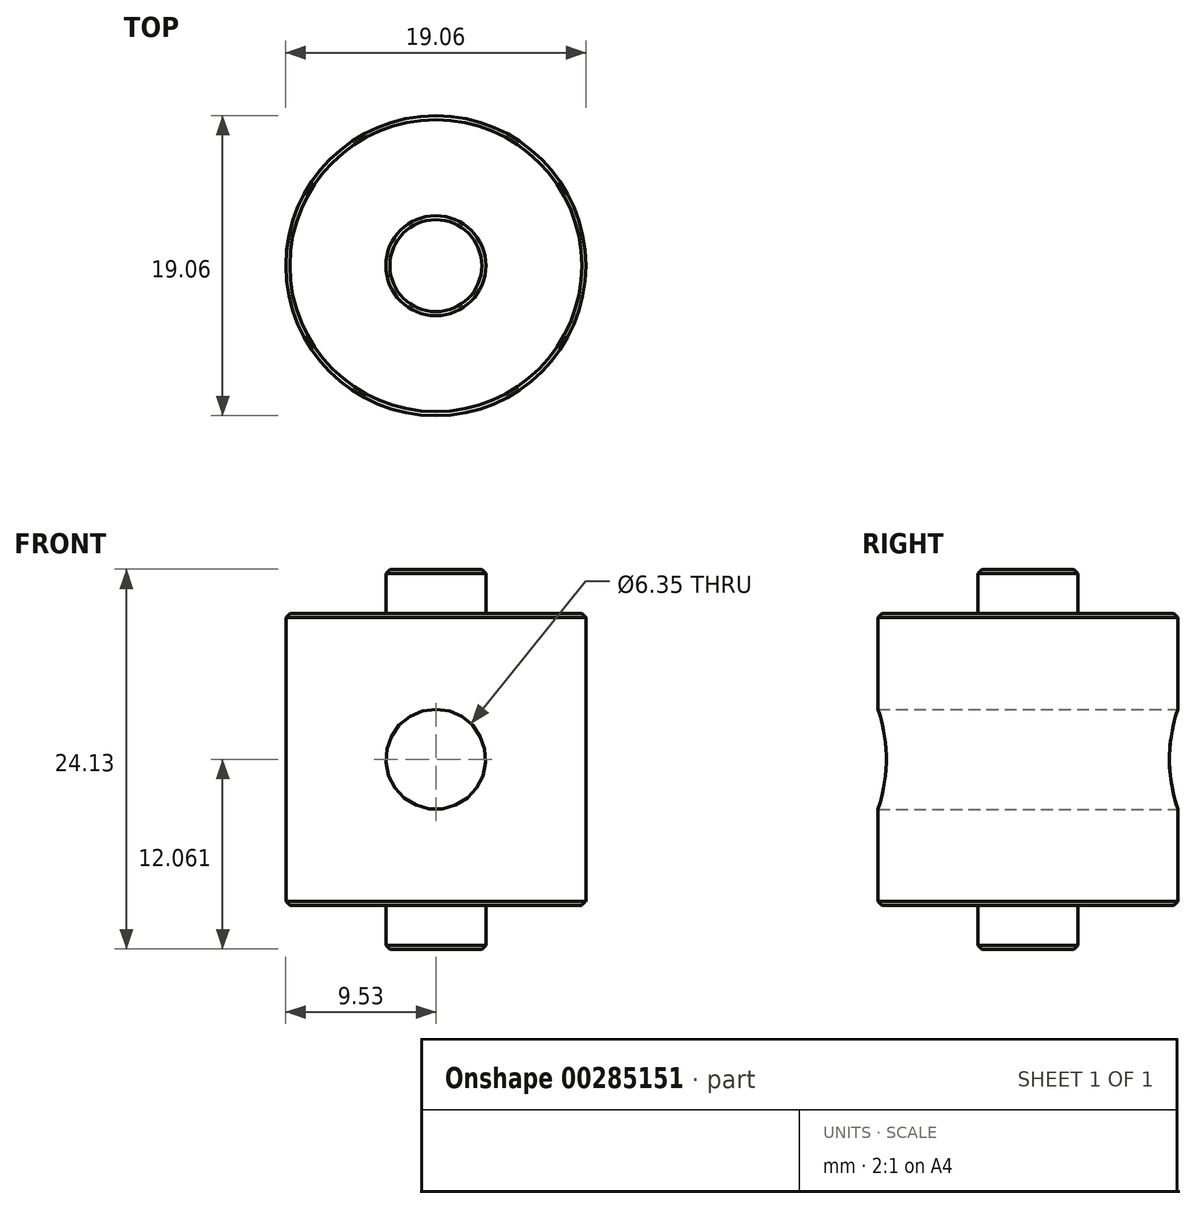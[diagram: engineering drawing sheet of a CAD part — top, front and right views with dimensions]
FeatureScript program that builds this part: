
annotation { "Feature Type Name" : "Feature", "Feature Type Description" : "" }
export const myFeature = defineFeature(function(context is Context, id is Id, definition is map)
    precondition{}
    {
        {
            var Q0;
            Q0=qCreatedBy(makeId("Top.planeOp"),FACE);
            var sketch = newSketch(context, id + "F0", { "sketchPlane" : qUnion([Q0])});
            skCircle(sketch, "E0", {"center": v(0, 0) * mm, "radius": 9.53 * mm});
            skSolve(sketch);
        }
        {
            var Q0;
            Q0=makeQuery(id+"F0.imprint","IMPRINT",FACE,{"disambiguationData":[TD([[makeQuery(id+"F0.imprint","IMPRINT",EDGE,{"derivedFrom":sQuery(id+"F0.wireOp",EDGE,"E0")}),1.0]])]});
            extrude(context, id + "F1", {"entities" : qUnion([Q0]), "depth" : 18.54 * mm});
        }
        {
            var Q0;
            Q0=makeQuery(id+"F1.opExtrude","CAP_FACE",FACE,{"disambiguationData":[OSD([sQuery(id+"F0.wireOp",EDGE,"E0")])],"isStart":false});
            var sketch = newSketch(context, id + "F2", { "sketchPlane" : qUnion([Q0])});
            skCircle(sketch, "E1", {"center": v(0, 0) * mm, "radius": 3.18 * mm});
            skSolve(sketch);
        }
        {
            var Q0;
            Q0=makeQuery(id+"F2.imprint","IMPRINT",FACE,{"disambiguationData":[TD([[makeQuery(id+"F2.imprint","IMPRINT",EDGE,{"derivedFrom":sQuery(id+"F2.wireOp",EDGE,"E1")}),1.0]])]});
            extrude(context, id + "F3", {"entities" : qUnion([Q0]), "operationType" : NewBodyOperationType.ADD, "depth" : 2.8 * mm});
        }
        {
            var Q0;
            Q0=makeQuery(id+"F1.opExtrude","CAP_FACE",FACE,{"disambiguationData":[OSD([sQuery(id+"F0.wireOp",EDGE,"E0")])],"isStart":true});
            var sketch = newSketch(context, id + "F4", { "sketchPlane" : qUnion([Q0])});
            skCircle(sketch, "E2", {"center": v(0, 0) * mm, "radius": 3.18 * mm});
            skSolve(sketch);
        }
        {
            var Q0;
            Q0 = qSketchRegion(id + "F4", true);
            extrude(context, id + "F5", {"entities" : qUnion([Q0]), "operationType" : NewBodyOperationType.ADD, "depth" : 2.8 * mm});
        }
        {
            var Q0;
            Q0=qCreatedBy(makeId("Front.planeOp"),FACE);
            var sketch = newSketch(context, id + "F6", { "sketchPlane" : qUnion([Q0])});
            skLineSegment(sketch, "E3", {"start": v(-9.53, 0) * mm, "end": v(-9.53, 18.54) * mm, "construction": true});
            skLineSegment(sketch, "E4", {"start": v(9.53, 18.54) * mm, "end": v(9.53, 0) * mm, "construction": true});
            skLineSegment(sketch, "E5", {"start": v(-9.53, 18.54) * mm, "end": v(9.53, 0) * mm, "construction": true});
            skCircle(sketch, "E6", {"center": v(0, 9.27) * mm, "radius": 3.18 * mm});
            skSolve(sketch);
        }
        {
            var Q0;
            Q0 = qSketchRegion(id + "F6", true);
            extrude(context, id + "F7", {"entities" : qUnion([Q0]), "operationType" : NewBodyOperationType.REMOVE, "depth" : 25.4 * mm, "hasSecondDirection" : true, "secondDirectionOppositeDirection" : true, "secondDirectionDepth" : 25.4 * mm});
        }
        {
            var Q0;
            Q0=makeQuery(id+"F1.opExtrude","CAP_EDGE",EDGE,{"disambiguationData":[OSD([sQuery(id+"F0.wireOp",EDGE,"E0")])],"isStart":false});
            var Q1;
            Q1=makeQuery(id+"F3.opExtrude","CAP_EDGE",EDGE,{"disambiguationData":[OSD([sQuery(id+"F2.wireOp",EDGE,"E1")])],"isStart":false});
            var Q2;
            Q2=makeQuery(id+"F1.opExtrude","CAP_EDGE",EDGE,{"disambiguationData":[OSD([sQuery(id+"F0.wireOp",EDGE,"E0")])],"isStart":true});
            var Q3;
            Q3=makeQuery(id+"F5.opExtrude","CAP_EDGE",EDGE,{"disambiguationData":[OSD([sQuery(id+"F4.wireOp",EDGE,"E2")])],"isStart":false});
            chamfer(context, id + "F8", {"entities" : qUnion([Q0, Q1, Q2, Q3]), "width" : 0.25 * mm, "tangentPropagation" : true});
        }
    });
